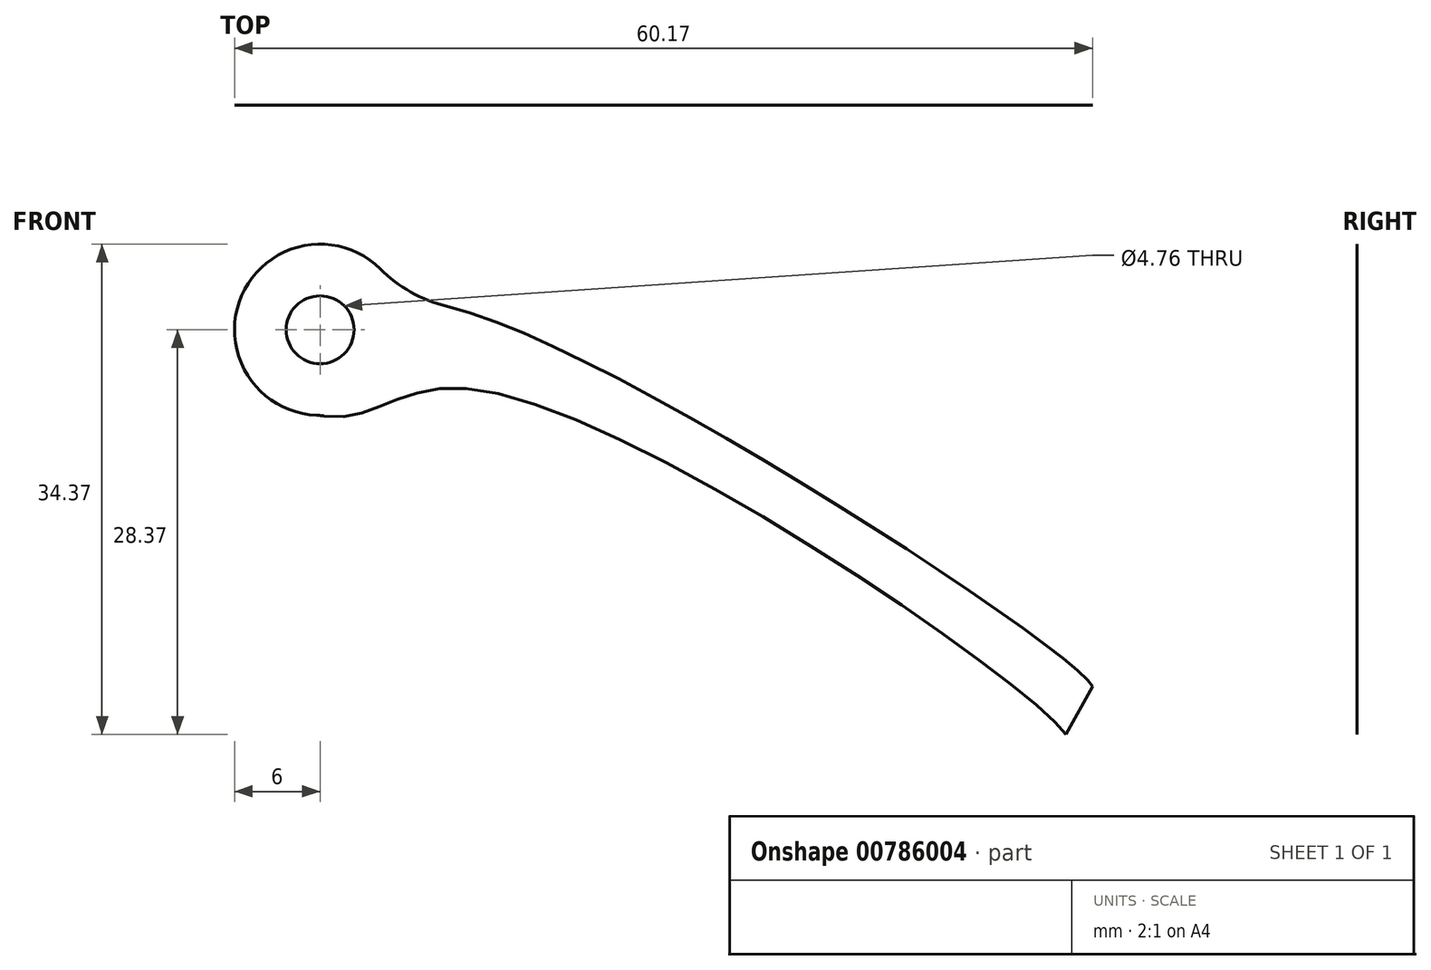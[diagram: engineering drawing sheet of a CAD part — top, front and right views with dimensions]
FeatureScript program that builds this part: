
annotation { "Feature Type Name" : "Feature", "Feature Type Description" : "" }
export const myFeature = defineFeature(function(context is Context, id is Id, definition is map)
    precondition{}
    {
        {
            var Q0;
            Q0=qCreatedBy(makeId("Front.planeOp"),FACE);
            var sketch = newSketch(context, id + "F0", { "sketchPlane" : qUnion([Q0])});
            skCircle(sketch, "E0", {"center": v(0, 0) * mm, "radius": 2.38 * mm});
            skCircle(sketch, "E1", {"center": v(0, 0) * mm, "radius": 6 * mm});
            skFitSpline(sketch, "E2", {"points": [v(0, 0) * mm, v(16.8, -1.38) * mm, v(54.17, -25.02) * mm], "startDerivative": vector(25.87, 26.74) * mm, "endDerivative": vector(5.59, -11.03) * mm});
            skFitSpline(sketch, "E3", {"points": [v(0, -6) * mm, v(11.08, -4.2) * mm, v(52.3, -28.37) * mm], "startDerivative": vector(35.12, -6.69) * mm, "endDerivative": vector(10.64, -15.64) * mm});
            skLineSegment(sketch, "E4", {"start": v(54.17, -25.02) * mm, "end": v(52.3, -28.37) * mm});
            skSolve(sketch);
        }
        {
            var Q0;
            Q0=qSketchRegion(id+"F0",true);
            extrude(context, id + "F1", {"entities" : qUnion([Q0]), "depth" : 1 / 203.2 * mm, "offsetDistance" : 25 * mm});
        }
        {
            var Q0;
            Q0=makeQuery(id+"F1.opExtrude","SWEPT_EDGE",EDGE,{"disambiguationData":[OSD([sQuery(id+"F0.wireOp",EDGE,"E1"),sQuery(id+"F0.wireOp",EDGE,"E2")])]});
            fillet(context, id + "F2", {"entities" : qUnion([Q0]), "radius" : 10 * mm, "tangentPropagation" : true, "allowEdgeOverflow" : false});
        }
        {
            var Q0;
            Q0=makeQuery(id+"F1.opExtrude","SWEPT_EDGE",EDGE,{"disambiguationData":[OSD([sQuery(id+"F0.wireOp",EDGE,"E1"),sQuery(id+"F0.wireOp",EDGE,"E3")])]});
            fillet(context, id + "F3", {"entities" : qUnion([Q0]), "radius" : 5 * mm, "tangentPropagation" : true, "allowEdgeOverflow" : false});
        }
    });
